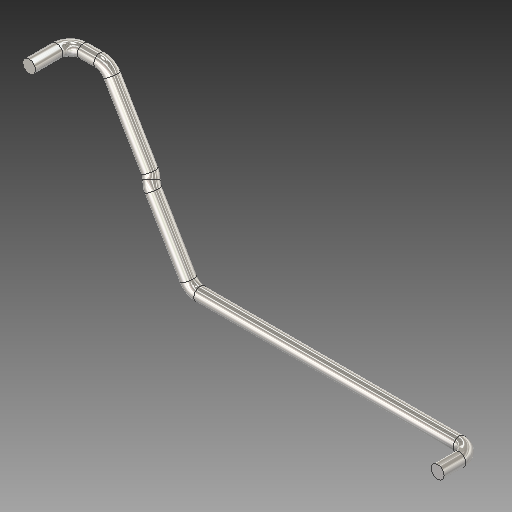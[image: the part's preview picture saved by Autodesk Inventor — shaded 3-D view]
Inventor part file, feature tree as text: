
AUTODESK INVENTOR PART (.ipt)
format: ipt  version: 2019 (Build 230136000, 136)  size: 161,792 bytes
history: native  units: in
note: dims shown in document units (in); Inventor stores cm internally (conversion verified against a paired STEP export)
features: sketch x10, other x8, plane x5
ambient origin geometry x8: Origin, YZ Plane, XZ Plane, XY Plane, X Axis, Y Axis, Z Axis, Center Point
bodies: Solid1 (feature_tree)
feature tree (23):
  other  "Side Link Bar.ipt"
  other  "Solid1::Side Link Bar.ipt"
  other  "TaggingFeature1"
  sketch  "Sketch1"  dims[d0=0.3937in]
  sketch  "Sketch2"
  sketch  "Sketch3"
  sketch  "Sketch4"
  sketch  "Sketch5"
  sketch  "Sketch6"
  sketch  "Sketch7"
  sketch  "Sketch8"
  sketch  "Sketch10"
  sketch  "Sketch11"
  plane  "Work Plane1"
  plane  "Work Plane2"
  plane  "Work Plane3"
  plane  "Work Plane4"
  plane  "Work Plane5"
  other  "Work Axis1"
  other  "Work Axis2"
  other  "Work Axis3"
  other  "Work Axis4"
  other  "Work Axis5"
